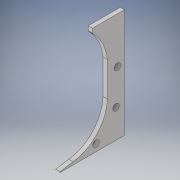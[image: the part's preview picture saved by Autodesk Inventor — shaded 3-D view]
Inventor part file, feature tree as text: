
AUTODESK INVENTOR PART (.ipt)
format: ipt  version: 2018 (Build 220112000, 112)  size: 156,672 bytes
history: native  units: in
note: dims shown in document units (in); Inventor stores cm internally (conversion verified against a paired STEP export)
features: fillet x2, sketch x2, extrude x1, hole x1
ambient origin geometry x8: Origin, YZ Plane, XZ Plane, XY Plane, X Axis, Y Axis, Z Axis, Center Point
bodies: Solid1 (feature_tree)
feature tree (6):
  extrude  "Extrusion1"  Depth=12.0in
  fillet  "Fillet1"  Radius=19.0in
  fillet  "Fillet2"  Radius=3.0in
  hole  "Hole1"  [1 undecoded]
  sketch  "Sketch1"  dims[d0=13.0in d1=12.0in d2=19.0in d3=3.0in]
  sketch  "Sketch2"  dims[d4=6.0in d5=8.25in d9=9.0in d13=8.625in d16=0.268in d17=0.134in d19=3.0in d20=3.0in d25=0.5in d39=7.5in d40=6.0in d41=0.5in d42=6.375in d43=135.0deg d44=7.0in d45=0.75in d46=0.0in d47=0.0625in d48=0.125in d49=5.0in d50=1.25in d51=2.0in d52=1.5in d53=4.0in d54=11.0in d55=4.0in d56=1.25in d57=5.0in d58=1.125in d59=0.75in d60=0.375in d61=0.25in d62=0.5635in d63=1.0in d64=0.8108in]
note: 1 required parameter value undecoded (feature->parameter linkage not recoverable at this tier; creation-order binding heuristic only, values carry confidence <= 0.55)
